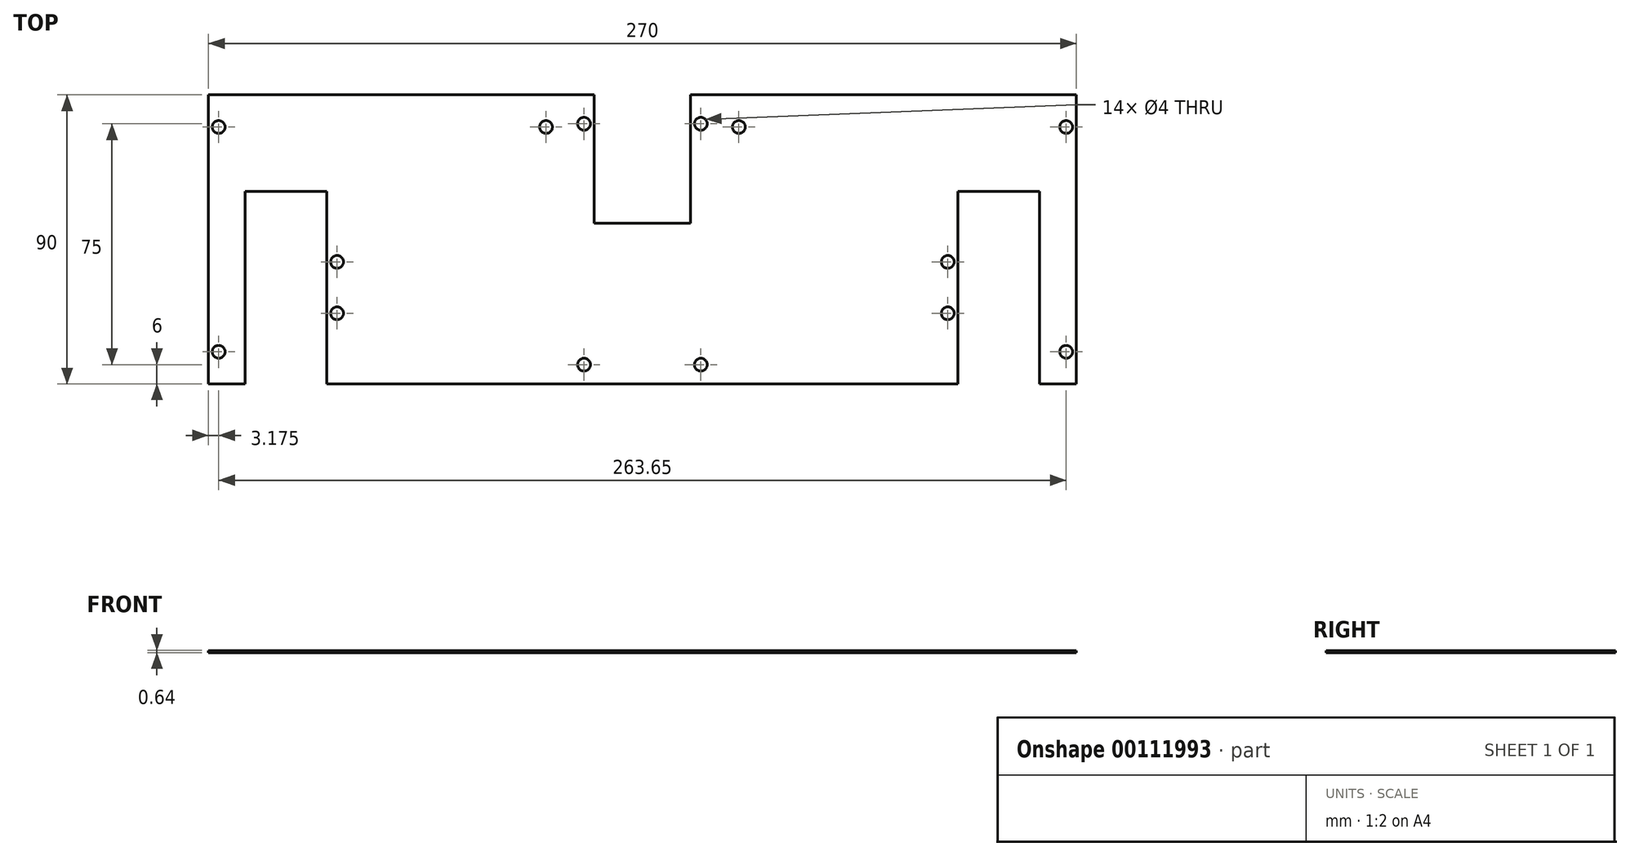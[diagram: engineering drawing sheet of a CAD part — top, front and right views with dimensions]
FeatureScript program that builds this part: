
annotation { "Feature Type Name" : "Feature", "Feature Type Description" : "" }
export const myFeature = defineFeature(function(context is Context, id is Id, definition is map)
    precondition{}
    {
        {
            var Q0;
            Q0=qCreatedBy(makeId("Top.planeOp"),FACE);
            var sketch = newSketch(context, id + "F0", { "sketchPlane" : qUnion([Q0])});
            skLineSegment(sketch, "E0.bottom", {"start": v(0, 0) * mm, "end": v(270, 0) * mm});
            skLineSegment(sketch, "E0.top", {"start": v(0, -90) * mm, "end": v(270, -90) * mm});
            skLineSegment(sketch, "E0.left", {"start": v(0, 0) * mm, "end": v(0, -90) * mm});
            skLineSegment(sketch, "E0.right", {"start": v(270, 0) * mm, "end": v(270, -90) * mm});
            skLineSegment(sketch, "E1", {"start": v(135, 0) * mm, "end": v(135, -90) * mm, "construction": true});
            skCircle(sketch, "E2", {"center": v(116.83, -9) * mm, "radius": 2 * mm});
            skCircle(sketch, "E3", {"center": v(153.18, -9) * mm, "radius": 2 * mm});
            skCircle(sketch, "E4", {"center": v(153.18, -84) * mm, "radius": 2 * mm});
            skCircle(sketch, "E5", {"center": v(116.83, -84) * mm, "radius": 2 * mm});
            skLineSegment(sketch, "E6", {"start": v(116.83, -9) * mm, "end": v(135, -9) * mm, "construction": true});
            skLineSegment(sketch, "E7", {"start": v(135, -9) * mm, "end": v(153.18, -9) * mm, "construction": true});
            skCircle(sketch, "E8", {"center": v(105, -10) * mm, "radius": 2 * mm});
            skCircle(sketch, "E9", {"center": v(165, -10) * mm, "radius": 2 * mm});
            skCircle(sketch, "E10", {"center": v(266.83, -10) * mm, "radius": 2 * mm});
            skCircle(sketch, "E11", {"center": v(266.82, -80) * mm, "radius": 2 * mm});
            skCircle(sketch, "E12", {"center": v(3.18, -80) * mm, "radius": 2 * mm});
            skCircle(sketch, "E13", {"center": v(3.17, -10) * mm, "radius": 2 * mm});
            skLineSegment(sketch, "E14.bottom", {"start": v(3.17, -10) * mm, "end": v(266.83, -10) * mm, "construction": true});
            skLineSegment(sketch, "E14.top", {"start": v(3.18, -80) * mm, "end": v(266.82, -80) * mm, "construction": true});
            skLineSegment(sketch, "E14.left", {"start": v(3.17, -10) * mm, "end": v(3.18, -80) * mm, "construction": true});
            skLineSegment(sketch, "E14.right", {"start": v(266.82, -10) * mm, "end": v(266.82, -80) * mm, "construction": true});
            skLineSegment(sketch, "E15.bottom", {"start": v(105, -10) * mm, "end": v(165, -10) * mm, "construction": true});
            skLineSegment(sketch, "E15.top", {"start": v(105, -26) * mm, "end": v(165, -26) * mm, "construction": true});
            skLineSegment(sketch, "E15.left", {"start": v(105, -10) * mm, "end": v(105, -26) * mm, "construction": true});
            skLineSegment(sketch, "E15.right", {"start": v(165, -10) * mm, "end": v(165, -26) * mm, "construction": true});
            skLineSegment(sketch, "E16", {"start": v(3.17, -10) * mm, "end": v(0, -10) * mm, "construction": true});
            skLineSegment(sketch, "E17", {"start": v(266.83, -10) * mm, "end": v(270, -10) * mm, "construction": true});
            skPoint(sketch, "E18", {"position": v(135, -10) * mm});
            skLineSegment(sketch, "E19.bottom", {"start": v(40, -52) * mm, "end": v(230, -52) * mm, "construction": true});
            skLineSegment(sketch, "E19.top", {"start": v(40, -68) * mm, "end": v(230, -68) * mm, "construction": true});
            skLineSegment(sketch, "E19.left", {"start": v(40, -52) * mm, "end": v(40, -68) * mm, "construction": true});
            skLineSegment(sketch, "E19.right", {"start": v(230, -52) * mm, "end": v(230, -68) * mm, "construction": true});
            skPoint(sketch, "E20", {"position": v(40, -60) * mm});
            skPoint(sketch, "E21", {"position": v(135, -68) * mm});
            skCircle(sketch, "E22", {"center": v(40, -52) * mm, "radius": 2 * mm});
            skCircle(sketch, "E23", {"center": v(40, -68) * mm, "radius": 2 * mm});
            skCircle(sketch, "E24", {"center": v(230, -68) * mm, "radius": 2 * mm});
            skCircle(sketch, "E25", {"center": v(230, -52) * mm, "radius": 2 * mm});
            skSolve(sketch);
        }
        {
            var Q0;
            Q0 = qSketchRegion(id + "F0", true);
            extrude(context, id + "F1", {"entities" : qUnion([Q0]), "depth" : 0.64 * mm});
        }
        {
            var Q0;
            Q0=makeQuery(id+"F1.opExtrude","CAP_FACE",FACE,{"disambiguationData":[OSD([sQuery(id+"F0.wireOp",EDGE,"E0.bottom"),sQuery(id+"F0.wireOp",EDGE,"E0.top"),sQuery(id+"F0.wireOp",EDGE,"E0.left"),sQuery(id+"F0.wireOp",EDGE,"E0.right"),sQuery(id+"F0.wireOp",EDGE,"E2"),sQuery(id+"F0.wireOp",EDGE,"E3"),sQuery(id+"F0.wireOp",EDGE,"E4"),sQuery(id+"F0.wireOp",EDGE,"E5"),sQuery(id+"F0.wireOp",EDGE,"E8"),sQuery(id+"F0.wireOp",EDGE,"WELkqFth-3o0o-ftXi-utei-kRQcHvHYL5um"),sQuery(id+"F0.wireOp",EDGE,"E9"),sQuery(id+"F0.wireOp",EDGE,"eXVsyTL1-Jg9m-HL9v-4Vqq-pGn0sDnhwVNd"),sQuery(id+"F0.wireOp",EDGE,"E10"),sQuery(id+"F0.wireOp",EDGE,"E11"),sQuery(id+"F0.wireOp",EDGE,"E12"),sQuery(id+"F0.wireOp",EDGE,"E13")])],"isStart":false});
            var sketch = newSketch(context, id + "F2", { "sketchPlane" : qUnion([Q0])});
            skLineSegment(sketch, "E26.bottom", {"start": v(120, 0) * mm, "end": v(150, 0) * mm});
            skLineSegment(sketch, "E26.top", {"start": v(120, -40) * mm, "end": v(150, -40) * mm});
            skLineSegment(sketch, "E26.left", {"start": v(120, 0) * mm, "end": v(120, -40) * mm});
            skLineSegment(sketch, "E26.right", {"start": v(150, 0) * mm, "end": v(150, -40) * mm});
            skLineSegment(sketch, "E27", {"start": v(135, -90) * mm, "end": v(135, -40) * mm, "construction": true});
            skLineSegment(sketch, "E28.bottom", {"start": v(36.82, -30) * mm, "end": v(11.42, -30) * mm});
            skLineSegment(sketch, "E28.top", {"start": v(36.82, -90) * mm, "end": v(11.42, -90) * mm});
            skLineSegment(sketch, "E28.left", {"start": v(36.82, -30) * mm, "end": v(36.82, -90) * mm});
            skLineSegment(sketch, "E28.right", {"start": v(11.42, -30) * mm, "end": v(11.42, -90) * mm});
            skLineSegment(sketch, "E29.bottom", {"start": v(233.18, -30) * mm, "end": v(258.58, -30) * mm});
            skLineSegment(sketch, "E29.top", {"start": v(233.18, -90) * mm, "end": v(258.58, -90) * mm});
            skLineSegment(sketch, "E29.left", {"start": v(233.18, -30) * mm, "end": v(233.18, -90) * mm});
            skLineSegment(sketch, "E29.right", {"start": v(258.58, -30) * mm, "end": v(258.58, -90) * mm});
            skLineSegment(sketch, "E30", {"start": v(36.82, -30) * mm, "end": v(233.18, -30) * mm, "construction": true});
            skPoint(sketch, "E31", {"position": v(135, -30) * mm});
            skPoint(sketch, "E32", {"position": v(36.82, -60) * mm});
            skLineSegment(sketch, "E33", {"start": v(40, -52) * mm, "end": v(40, -68) * mm, "construction": true});
            skPoint(sketch, "E34", {"position": v(40, -60) * mm});
            skSolve(sketch);
        }
        {
            var Q0;
            Q0 = qSketchRegion(id + "F2", true);
            extrude(context, id + "F3", {"entities" : qUnion([Q0]), "operationType" : NewBodyOperationType.REMOVE, "endBound" : BoundingType.THROUGH_ALL, "oppositeDirection" : true, "depth" : 25 * mm});
        }
    });
